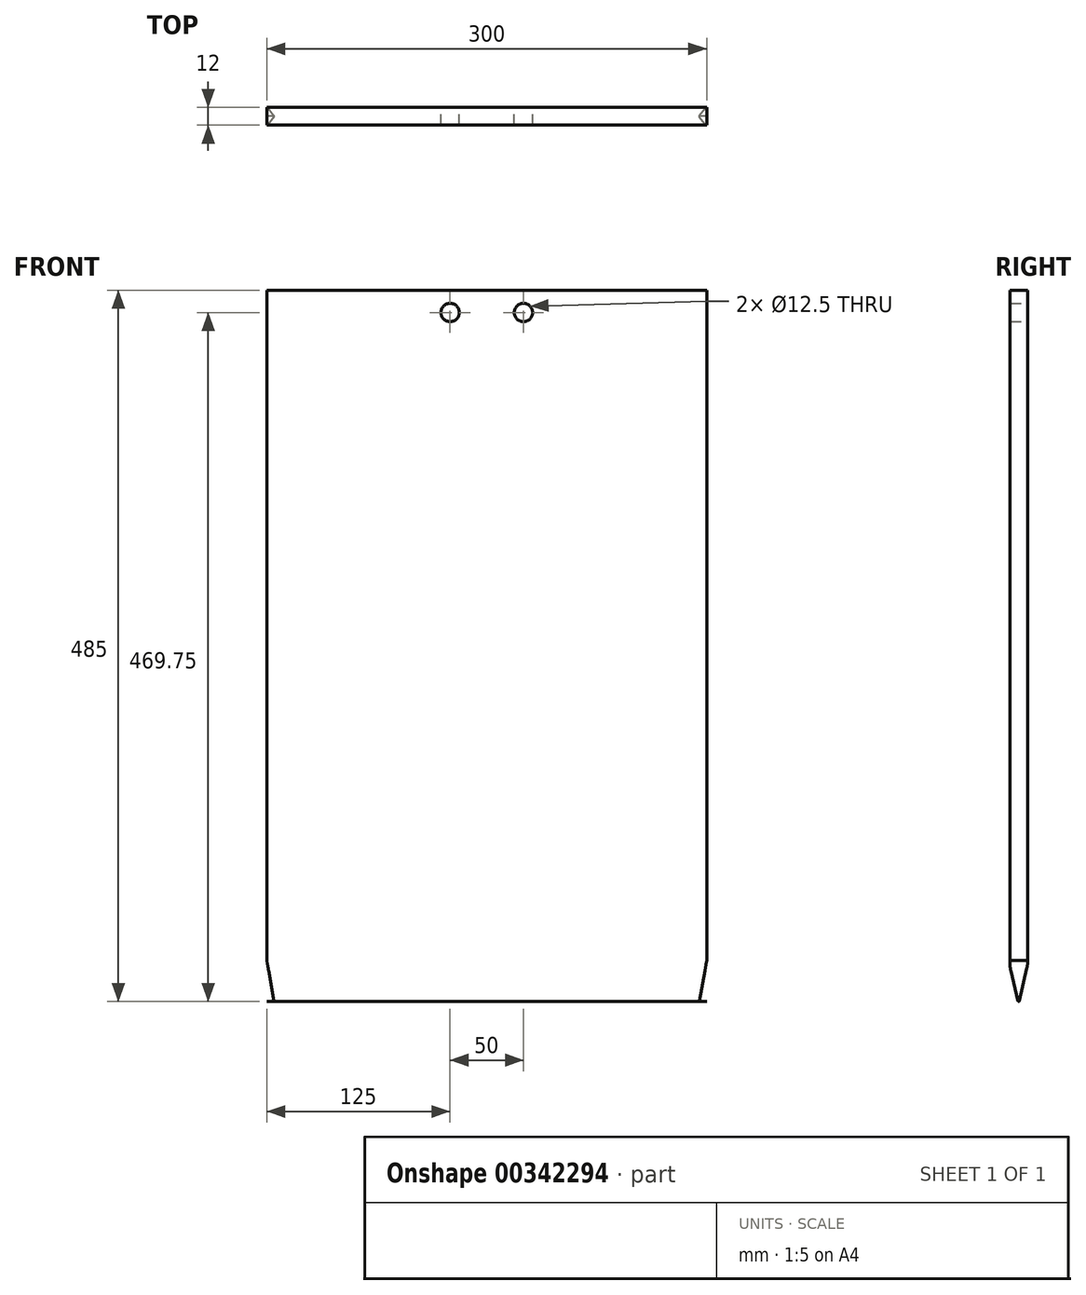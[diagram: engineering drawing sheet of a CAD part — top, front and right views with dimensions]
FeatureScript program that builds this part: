
annotation { "Feature Type Name" : "Feature", "Feature Type Description" : "" }
export const myFeature = defineFeature(function(context is Context, id is Id, definition is map)
    precondition{}
    {
        {
            var Q0;
            Q0=qCreatedBy(makeId("Right.planeOp"),FACE);
            var sketch = newSketch(context, id + "F0", { "sketchPlane" : qUnion([Q0])});
            skLineSegment(sketch, "E0.bottom", {"start": v(6, 242.5) * mm, "end": v(-6, 242.5) * mm});
            skLineSegment(sketch, "E0.top", {"start": v(6, -242.5) * mm, "end": v(-6, -242.5) * mm});
            skLineSegment(sketch, "E0.left", {"start": v(6, 242.5) * mm, "end": v(6, -215.29) * mm});
            skLineSegment(sketch, "E0.right", {"start": v(-6, 242.5) * mm, "end": v(-6, -216.95) * mm});
            skPoint(sketch, "E0.middle", {"position": v(0, 0) * mm});
            skPoint(sketch, "E1", {"position": v(0, -242.5) * mm});
            skCircle(sketch, "E2", {"center": v(0, -242) * mm, "radius": 0.5 * mm});
            skLineSegment(sketch, "E3", {"start": v(-5.44, -221.65) * mm, "end": v(-0.49, -242.12) * mm});
            skLineSegment(sketch, "E4", {"start": v(0.49, -242.1) * mm, "end": v(5.52, -219.66) * mm});
            skPoint(sketch, "E5.newPointB", {"position": v(-6.44, -217.5) * mm});
            skArc(sketch, "E5.filletArc", {"start": v(-6, -216.95) * mm, "mid": v(-5.86, -219.32) * mm, "end": v(-5.44, -221.65) * mm});
            skPoint(sketch, "E6.newPointA", {"position": v(6, -242.5) * mm});
            skPoint(sketch, "E6.newPointB", {"position": v(6, -217.5) * mm});
            skArc(sketch, "E6.filletArc", {"start": v(5.52, -219.66) * mm, "mid": v(5.88, -217.49) * mm, "end": v(6, -215.29) * mm});
            skSolve(sketch);
        }
        {
            var Q0;
            {var subQ4=sQuery(id+"F0.wireOp",EDGE,"E0.bottom");Q0=makeQuery(id+"F0.imprint","IMPRINT",FACE,{"disambiguationData":[TD([[makeQuery(id+"F0.imprint","IMPRINT",EDGE,{"derivedFrom":subQ4}),1.0]])]});}
            var Q1;
            {var subQ0=sQuery(id+"F0.wireOp",EDGE,"E2");var subQ1=makeQuery(id+"F0.imprint","INTERSECT",VERTEX,{"derivedFrom":[subQ0,sQuery(id+"F0.wireOp",EDGE,"E3")]});Q1=makeQuery(id+"F0.imprint","IMPRINT",FACE,{"disambiguationData":[TD([[makeQuery(id+"F0.imprint","IMPRINT",EDGE,{"disambiguationData":[TD([[subQ1,-1.0]])],"derivedFrom":subQ0}),1.0]])]});}
            extrude(context, id + "F1", {"entities" : qUnion([Q0, Q1]), "endBound" : BoundingType.SYMMETRIC, "depth" : 300 * mm, "offsetDistance" : 25 * mm});
        }
        {
            var Q0;
            Q0=makeQuery(id+"F1.opExtrude","SWEPT_FACE",FACE,{"disambiguationData":[OSD([sQuery(id+"F0.wireOp",EDGE,"E0.left")])]});
            var sketch = newSketch(context, id + "F2", { "sketchPlane" : qUnion([Q0])});
            skCircle(sketch, "E7", {"center": v(25, 227.25) * mm, "radius": 6.25 * mm});
            skCircle(sketch, "E8", {"center": v(-25, 227.25) * mm, "radius": 6.25 * mm});
            skLineSegment(sketch, "E9", {"start": v(-150, -214.5) * mm, "end": v(-145, -242.5) * mm});
            skLineSegment(sketch, "E10", {"start": v(-150.1, -242.5) * mm, "end": v(-145, -242.5) * mm});
            skLineSegment(sketch, "E11", {"start": v(-150, -214.5) * mm, "end": v(-150.1, -242.5) * mm});
            skLineSegment(sketch, "E12.MirrorCS", {"start": v(150, -214.5) * mm, "end": v(145, -242.5) * mm});
            skLineSegment(sketch, "E13.MirrorCS", {"start": v(150, -214.5) * mm, "end": v(150.1, -242.5) * mm});
            skLineSegment(sketch, "E14.MirrorCS", {"start": v(150.1, -242.5) * mm, "end": v(145, -242.5) * mm});
            skLineSegment(sketch, "E15", {"start": v(-78.85, 227.25) * mm, "end": v(113.62, 227.25) * mm});
            skPoint(sketch, "E16", {"position": v(0, 227.25) * mm});
            skSolve(sketch);
        }
        {
            var Q0;
            Q0=qSketchRegion(id+"F2",true);
            extrude(context, id + "F3", {"entities" : qUnion([Q0]), "operationType" : NewBodyOperationType.REMOVE, "oppositeDirection" : true, "depth" : 25 * mm});
        }
    });
